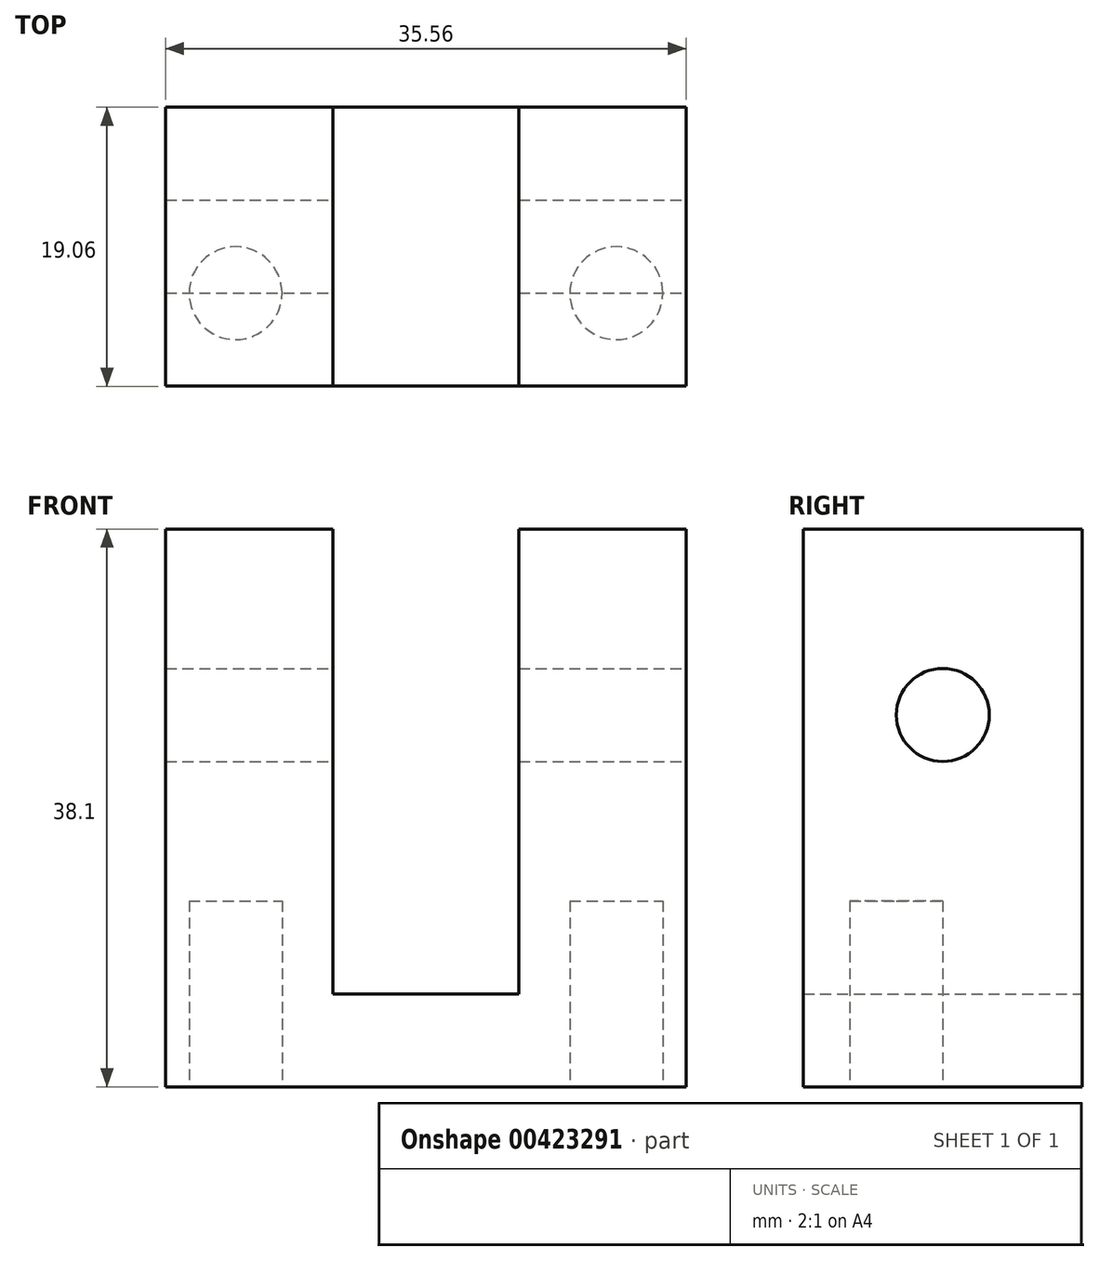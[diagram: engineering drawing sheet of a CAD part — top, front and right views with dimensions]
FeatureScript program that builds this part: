
annotation { "Feature Type Name" : "Feature", "Feature Type Description" : "" }
export const myFeature = defineFeature(function(context is Context, id is Id, definition is map)
    precondition{}
    {
        {
            var Q0;
            Q0=qCreatedBy(makeId("Front.planeOp"),FACE);
            var sketch = newSketch(context, id + "F0", { "sketchPlane" : qUnion([Q0])});
            skLineSegment(sketch, "E0.bottom", {"start": v(-17.78, 38.1) * mm, "end": v(-6.35, 38.1) * mm});
            skLineSegment(sketch, "E0.top", {"start": v(-17.78, 0) * mm, "end": v(17.78, 0) * mm});
            skLineSegment(sketch, "E0.left", {"start": v(-17.78, 38.1) * mm, "end": v(-17.78, 0) * mm});
            skLineSegment(sketch, "E0.right", {"start": v(17.78, 38.1) * mm, "end": v(17.78, 0) * mm});
            skLineSegment(sketch, "E1.top", {"start": v(6.35, 6.35) * mm, "end": v(-6.35, 6.35) * mm});
            skLineSegment(sketch, "E1.left", {"start": v(6.35, 38.1) * mm, "end": v(6.35, 6.35) * mm});
            skLineSegment(sketch, "E1.right", {"start": v(-6.35, 38.1) * mm, "end": v(-6.35, 6.35) * mm});
            skLineSegment(sketch, "E2.trimOffspring", {"start": v(6.35, 38.1) * mm, "end": v(17.78, 38.1) * mm});
            skSolve(sketch);
        }
        {
            var Q0;
            Q0 = qSketchRegion(id + "F0", true);
            extrude(context, id + "F1", {"entities" : qUnion([Q0]), "endBound" : BoundingType.SYMMETRIC, "depth" : 19.05 * mm});
        }
        {
            var Q0;
            Q0=makeQuery(id+"F1.opExtrude","SWEPT_FACE",FACE,{"disambiguationData":[OSD([sQuery(id+"F0.wireOp",EDGE,"E0.right")])]});
            var sketch = newSketch(context, id + "F2", { "sketchPlane" : qUnion([Q0])});
            skCircle(sketch, "E3", {"center": v(0, 25.4) * mm, "radius": 3.18 * mm});
            skSolve(sketch);
        }
        {
            var Q0;
            Q0 = qSketchRegion(id + "F2", true);
            extrude(context, id + "F3", {"entities" : qUnion([Q0]), "operationType" : NewBodyOperationType.REMOVE, "endBound" : BoundingType.THROUGH_ALL, "oppositeDirection" : true, "depth" : 25.4 * mm});
        }
        {
            var Q0;
            Q0=makeQuery(id+"F1.opExtrude","SWEPT_FACE",FACE,{"disambiguationData":[OSD([sQuery(id+"F0.wireOp",EDGE,"E0.top")])]});
            var sketch = newSketch(context, id + "F4", { "sketchPlane" : qUnion([Q0])});
            skCircle(sketch, "E4", {"center": v(-13, 3.17) * mm, "radius": 3.18 * mm});
            skCircle(sketch, "E5", {"center": v(13, 3.17) * mm, "radius": 3.18 * mm});
            skSolve(sketch);
        }
        {
            var Q0;
            Q0 = qSketchRegion(id + "F4", true);
            extrude(context, id + "F5", {"entities" : qUnion([Q0]), "operationType" : NewBodyOperationType.REMOVE, "oppositeDirection" : true, "depth" : 12.7 * mm});
        }
    });
